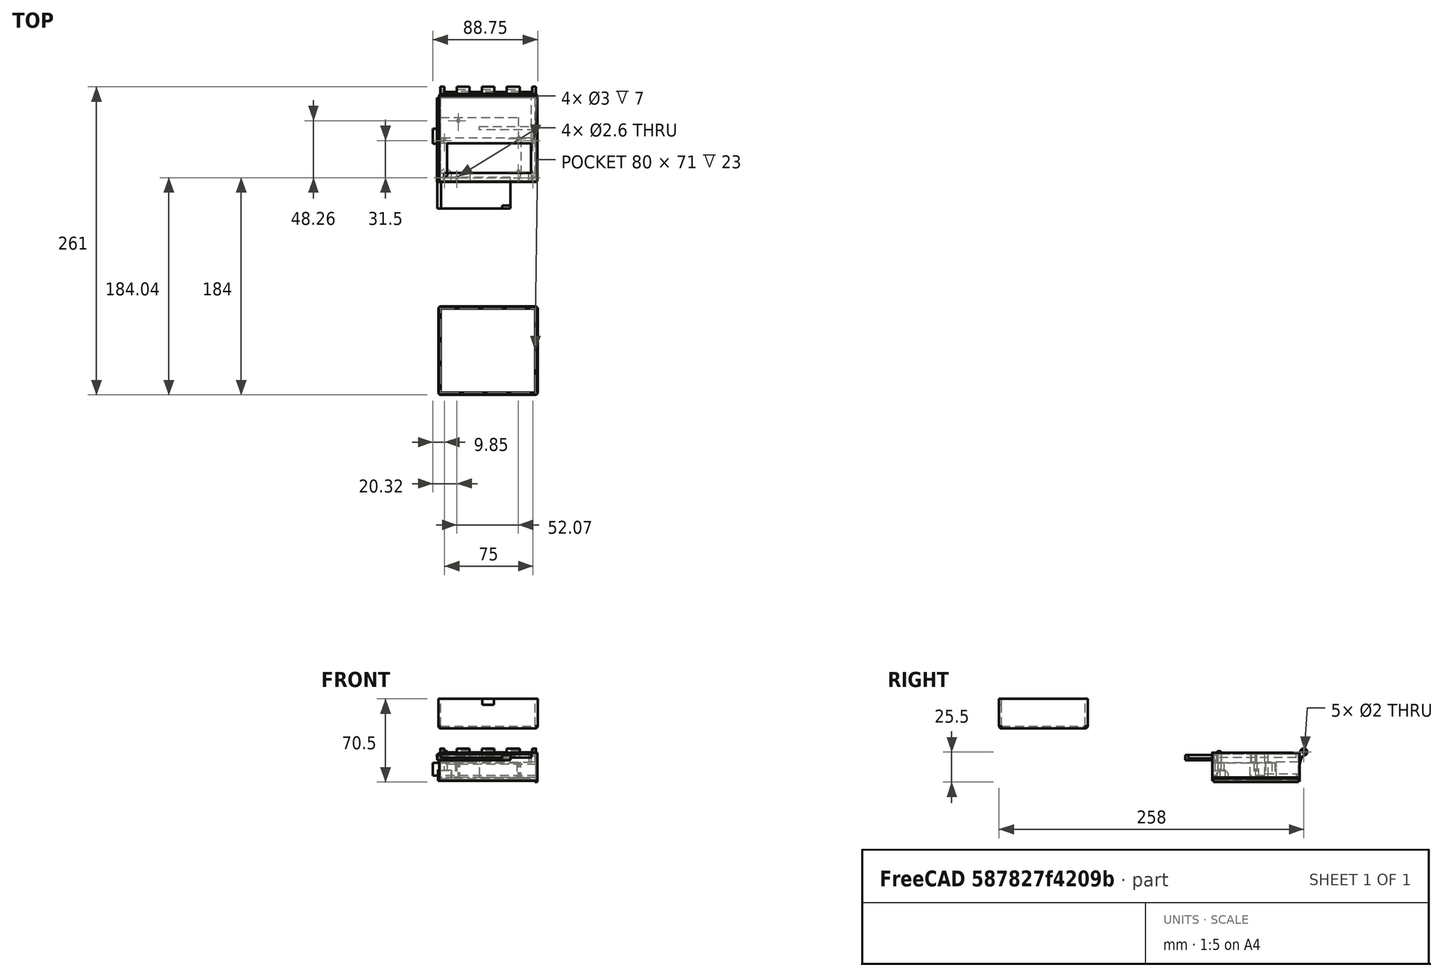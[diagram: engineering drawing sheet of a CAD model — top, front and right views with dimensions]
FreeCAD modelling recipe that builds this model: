
FCSTD DOCUMENT  (FreeCAD 1.0R39109 (Git))
Label: case_top_assembly
License: All rights reserved
LicenseURL: https://en.wikipedia.org/wiki/All_rights_reserved
objects: Sketcher::SketchObject×18, PartDesign::Pad×12, PartDesign::Pocket×8, PartDesign::SubShapeBinder×6, Mesh::Feature×5, PartDesign::Body×5, PartDesign::SubtractiveBox×4, PartDesign::Thickness×2, Part::FeaturePython×2, PartDesign::Fillet×1
note: 130 computed .brp shape members not serialized (recipe doc carries the construction recipe); baked Part::Feature solids carry a one-line shape summary decoded from their .brp

FEATURE [Mesh::Feature] Mesh001  label="power_switch_mesh"
  Placement = pos=(79,9,-82) rot=(0,0,-1;1.5708rad)
FEATURE [Mesh::Feature] Mesh002  label="display_mesh"
  Placement = pos=(-2,11,5) rot=(0,0,1;0rad)
FEATURE [Mesh::Feature] Mesh003  label="9V_Block_mesh"
  Placement = pos=(6,3,0.5) rot=(0,0,-1;1.5708rad)
FEATURE [PartDesign::SubShapeBinder] Binder
  BindCopyOnChange = 0
  BindMode = 0
  ClaimChildren = false
  Context = -> Body001 [Binder.]
  Fuse = false
  MakeFace = true
  OffsetFill = false
  OffsetIntersection = false
  OffsetJoinType = 0
  OffsetOpenResult = false
  PartialLoad = false
  Refine = true
  Relative = true
  Support = -> [b_Electronic_parts_001_003[Edge8,Edge5,Edge2,Edge1]]
  _Version = 2
FEATURE [PartDesign::SubShapeBinder] Binder001
  BindCopyOnChange = 0
  BindMode = 0
  ClaimChildren = false
  Context = -> Body001 [Binder001.]
  Fuse = false
  MakeFace = true
  Offset = 0.5
  OffsetFill = false
  OffsetIntersection = false
  OffsetJoinType = 0
  OffsetOpenResult = false
  PartialLoad = false
  Refine = true
  Relative = true
  Support = -> [b_Electronic_parts_001_002[Face18]]
  _Version = 2
FEATURE [PartDesign::SubShapeBinder] Binder002
  BindCopyOnChange = 0
  BindMode = 0
  ClaimChildren = false
  Context = -> Body001 [Binder002.]
  Fuse = false
  MakeFace = true
  OffsetFill = false
  OffsetIntersection = false
  OffsetJoinType = 0
  OffsetOpenResult = false
  PartialLoad = false
  Refine = true
  Relative = true
  Support = -> [b_Electronic_parts_001_002[Edge34,Edge33,Edge32,Edge31]]
  _Version = 2
FEATURE [Sketcher::SketchObject] Sketch007
  ArcFitTolerance = 1e-06
  AttachmentSupport = -> [XY_Plane001]
  FullyConstrained = true
  MakeInternals = false
  MapMode = 5
  sketch-geometry (4):
    g0: LineSegment StartX=-2.9 StartY=181 StartZ=0 EndX=-2.9 EndY=110 EndZ=0
    g1: LineSegment StartX=-2.9 StartY=110 StartZ=0 EndX=77.1 EndY=110 EndZ=0
    g2: LineSegment StartX=77.1 StartY=110 StartZ=0 EndX=77.1 EndY=181 EndZ=0
    g3: LineSegment StartX=77.1 StartY=181 StartZ=0 EndX=-2.9 EndY=181 EndZ=0
  constraints (10):
    c: Coincident(g0,g1)
    c: Coincident(g1,g2)
    c: Coincident(g2,g3)
    c: Coincident(g3,g0)
    c: Vertical(g0)
    c: Vertical(g2)
    c: Horizontal(g1)
    c: Horizontal(g3)
    c: Coincident(g0,g-4)
    c: Coincident(g1,g-5)
FEATURE [PartDesign::Pad] Pad004
  Direction = (0,0,1)
  Length = 23
  Length2 = 10
  Profile = -> Sketch007
  ReferenceAxis = -> Sketch007 [N_Axis]
  Refine = true
  Suppressed = false
  Type = 0
FEATURE [PartDesign::Thickness] Thickness001
  Base = -> Pad004 [Face6]
  BaseFeature = -> Pad004
  Intersection = false
  Join = 0
  Mode = 0
  Refine = true
  SupportTransform = false
  Suppressed = false
  Value = 2
FEATURE [PartDesign::Pocket] Pocket003
  BaseFeature = -> Thickness001
  Direction = (-1,0,0)
  Length = 5
  Length2 = 5
  Profile = -> Binder001
  Refine = true
  Suppressed = false
  Type = 0
FEATURE [PartDesign::Pocket] Pocket004
  BaseFeature = -> Pocket003
  Direction = (0,0,-1)
  Length = 0
  Length2 = 5
  Profile = -> Binder002
  Refine = true
  Suppressed = false
  Type = 3
  UpToFace = -> Pocket003 [Face19]
FEATURE [Sketcher::SketchObject] Sketch008
  ArcFitTolerance = 1e-06
  AttachmentSupport = -> [Pocket004]
  ExternalGeometry = -> [Pocket004]
  FullyConstrained = true
  MakeInternals = false
  MapMode = 5
  Placement = pos=(0,181,0) rot=(1,0,0;1.5708rad)
  sketch-geometry (6):
    g0: LineSegment StartX=32.1 StartY=23 StartZ=0 EndX=32.1 EndY=18 EndZ=0
    g1: LineSegment StartX=32.1 StartY=18 StartZ=0 EndX=42.1 EndY=18 EndZ=0
    g2: LineSegment StartX=42.1 StartY=18 StartZ=0 EndX=42.1 EndY=23 EndZ=0
    g3: LineSegment StartX=42.1 StartY=23 StartZ=0 EndX=32.1 EndY=23 EndZ=0
    g4: LineSegment [constr] StartX=-2.9 StartY=23 StartZ=0 EndX=32.1 EndY=23 EndZ=0
    g5: LineSegment [constr] StartX=42.1 StartY=23 StartZ=0 EndX=77.1 EndY=23 EndZ=0
  constraints (16):
    c: Coincident(g0,g1)
    c: Coincident(g1,g2)
    c: Coincident(g2,g3)
    c: Coincident(g3,g0)
    c: Vertical(g0)
    c: Vertical(g2)
    c: Horizontal(g1)
    c: Horizontal(g3)
    c: PointOnObject(g0,g-3)
    c: Coincident(g4,g-3)
    c: Coincident(g4,g0)
    c: Coincident(g5,g2)
    c: Coincident(g5,g-3)
    c: Equal(g5,g4)
    c: DistanceX(g1,g1) = 10
    c: DistanceY(g2,g2) = 5
FEATURE [PartDesign::Pocket] Pocket005
  BaseFeature = -> Pocket004
  Direction = (0,1,-2e-16)
  Length = 0
  Length2 = 5
  Profile = -> Sketch008
  ReferenceAxis = -> Sketch008 [N_Axis]
  Refine = true
  Suppressed = false
  Type = 3
  UpToFace = -> Pocket004 [Face14]
FEATURE [Part::FeaturePython] b_Electronic_parts_001_002  label="Electronic_parts_Eleego_002"  # a2plus imported part (geometry in sourceFile) (typed FeaturePython)
  a2p_Version = 0.4.68
  fixedPosition = true
  objectType = a2pPart
  sourceFile = ./Electronic_parts.FCStd
  sourcePart = Eleego
  subassemblyImport = false
  timeLastImport = 1.74161e+09
  updateColors = true
FEATURE [Part::FeaturePython] b_Electronic_parts_001_003  label="Electronic_parts_Keypad_002"  # a2plus imported part (geometry in sourceFile) (typed FeaturePython)
  Placement = pos=(-2.9,70,19.7) rot=(0,0,1;4.71239rad)
  a2p_Version = 0.4.68
  fixedPosition = false
  objectType = a2pPart
  sourceFile = ./Electronic_parts.FCStd
  sourcePart = Keypad
  subassemblyImport = false
  timeLastImport = 1.74161e+09
  updateColors = true
FEATURE [Sketcher::SketchObject] Sketch011
  ArcFitTolerance = 1e-06
  FullyConstrained = true
  MakeInternals = false
  MapMode = 5
  Placement = pos=(0,72,0) rot=(0,0.707107,0.707107;3.14159rad)
  sketch-geometry (12):
    g0: LineSegment StartX=-63.35 StartY=26 StartZ=0 EndX=-52.75 EndY=26 EndZ=0
    g1: LineSegment StartX=-21.35 StartY=26 StartZ=0 EndX=-10.75 EndY=26 EndZ=0
    g2: LineSegment StartX=-63.35 StartY=26 StartZ=0 EndX=-63.35 EndY=17.8 EndZ=0
    g3: LineSegment StartX=-52.75 StartY=26 StartZ=0 EndX=-52.75 EndY=17.8 EndZ=0
    g4: LineSegment StartX=-63.35 StartY=17.8 StartZ=0 EndX=-52.75 EndY=17.8 EndZ=0
    g5: LineSegment [constr] StartX=-74 StartY=26 StartZ=0 EndX=-63.35 EndY=26 EndZ=0
    g6: LineSegment [constr] StartX=-52.75 StartY=26 StartZ=0 EndX=-42.1 EndY=26 EndZ=0
    g7: LineSegment StartX=-21.35 StartY=26 StartZ=0 EndX=-21.35 EndY=17.8 EndZ=0
    g8: LineSegment StartX=-10.75 StartY=26 StartZ=0 EndX=-10.75 EndY=17.8 EndZ=0
    g9: LineSegment StartX=-21.35 StartY=17.8 StartZ=0 EndX=-10.75 EndY=17.8 EndZ=0
    g10: LineSegment [constr] StartX=-32.1 StartY=26 StartZ=0 EndX=-21.35 EndY=26 EndZ=0
    g11: LineSegment [constr] StartX=-10.75 StartY=26 StartZ=0 EndX=0 EndY=26 EndZ=0
  constraints (34):
    c: Horizontal(g0)
    c: Horizontal(g1)
    c: Horizontal(g-6,g0)
    c: Horizontal(g-3,g1)
    c: Distance(g-6,g-4) = 31.9
    c: Coincident(g2,g0)
    c: Vertical(g2)
    c: Coincident(g3,g0)
    c: Vertical(g3)
    c: Coincident(g4,g2)
    c: Coincident(g4,g3)
    c: Parallel(g4,g0)
    c: Coincident(g5,g-6)
    c: Coincident(g5,g0)
    c: Coincident(g6,g0)
    c: Coincident(g6,g-4)
    c: Equal(g5,g6)
    c: DistanceX(g4,g4) = 10.6
    c: Distance(g-6,g-6) = 5.45992
    c: Coincident(g7,g1)
    c: Vertical(g7)
    c: Coincident(g8,g1)
    c: Vertical(g8)
    c: Coincident(g9,g7)
    c: Coincident(g9,g8)
    c: Horizontal(g9)
    c: Coincident(g10,g-3)
    c: Coincident(g10,g1)
    c: Coincident(g11,g1)
    c: Coincident(g11,g-5)
    c: Equal(g11,g10)
    c: Equal(g3,g7)
    c: Equal(g1,g0)
    c: DistanceY(g7,g7) = 8.2
FEATURE [PartDesign::Pocket] Pocket007
  BaseFeature = -> Pocket005
  Direction = (0,-1,2e-16)
  Length = 9
  Length2 = 5
  Profile = -> Sketch011
  ReferenceAxis = -> Sketch011 [N_Axis]
  Refine = true
  Reversed = true
  Suppressed = false
  Type = 0
FEATURE [PartDesign::Body] Body001  label="case_bottom"
  AllowCompound = false
  Group = -> [Sketch007,Binder,Pad004,Thickness001,Binder001,Pocket003,Binder002,Pocket004,Sketch008,Pocket005,Sketch011,Pocket007]
  Origin = -> Origin001
  Placement = pos=(77.5,1.5,46.5) rot=(0,0,1;3.14159rad)
  Tip = -> Pocket007
FEATURE [PartDesign::SubShapeBinder] Binder004
  BindCopyOnChange = 0
  BindMode = 0
  ClaimChildren = false
  Context = -> Body002 [Binder004.]
  Fuse = false
  MakeFace = true
  OffsetFill = false
  OffsetIntersection = false
  OffsetJoinType = 0
  OffsetOpenResult = false
  PartialLoad = false
  Refine = true
  Relative = true
  _Version = 2
FEATURE [Sketcher::SketchObject] Sketch017
  ArcFitTolerance = 1e-06
  AttachmentSupport = -> [XY_Plane002]
  ExternalGeometry = -> [Binder004]
  FullyConstrained = true
  MakeInternals = false
  MapMode = 5
  sketch-geometry (4):
    g0: LineSegment StartX=-2.58093 StartY=2.78 StartZ=0 EndX=-2.58093 EndY=-23.72 EndZ=0
    g1: LineSegment StartX=-2.58093 StartY=-23.72 StartZ=0 EndX=59.4191 EndY=-23.72 EndZ=0
    g2: LineSegment StartX=59.4191 StartY=-23.72 StartZ=0 EndX=59.4191 EndY=2.78 EndZ=0
    g3: LineSegment StartX=59.4191 StartY=2.78 StartZ=0 EndX=-2.58093 EndY=2.78 EndZ=0
  constraints (11):
    c: Coincident(g0,g1)
    c: Coincident(g1,g2)
    c: Coincident(g2,g3)
    c: Coincident(g3,g0)
    c: Vertical(g0)
    c: Vertical(g2)
    c: Horizontal(g1)
    c: Horizontal(g3)
    c: Coincident(g0,g-4)
    c: PointOnObject(g1,g-5)
    c: Vertical(g-3,g2)
FEATURE [PartDesign::Pad] Pad008
  Direction = (0,0,1)
  Length = 1.5
  Length2 = 10
  Profile = -> Sketch017
  ReferenceAxis = -> Sketch017 [N_Axis]
  Refine = true
  Suppressed = false
  Type = 0
FEATURE [Sketcher::SketchObject] Sketch018
  ArcFitTolerance = 1e-06
  AttachmentSupport = -> [Pad008]
  ExternalGeometry = -> [Binder004]
  FullyConstrained = true
  MakeInternals = false
  MapMode = 5
  Placement = pos=(0,0,1.5) rot=(0,0,1;0rad)
  sketch-geometry (11):
    g0: LineSegment StartX=-2.58093 StartY=2.78 StartZ=0 EndX=-2.58093 EndY=-0.22 EndZ=0
    g1: LineSegment StartX=59.4191 StartY=-0.22 StartZ=0 EndX=59.4191 EndY=2.78 EndZ=0
    g2: LineSegment StartX=59.4191 StartY=2.78 StartZ=0 EndX=-2.58093 EndY=2.78 EndZ=0
    g3: LineSegment StartX=0.41907 StartY=-23.72 StartZ=0 EndX=0.41907 EndY=-0.22 EndZ=0
    g4: LineSegment StartX=-2.58093 StartY=-0.22 StartZ=0 EndX=-2.58093 EndY=-23.72 EndZ=0
    g5: LineSegment StartX=-2.58093 StartY=-23.72 StartZ=0 EndX=0.41907 EndY=-23.72 EndZ=0
    g6: LineSegment StartX=59.4191 StartY=-23.72 StartZ=0 EndX=59.4191 EndY=-21.22 EndZ=0
    g7: LineSegment StartX=59.4191 StartY=-21.22 StartZ=0 EndX=52.4191 EndY=-21.22 EndZ=0
    g8: LineSegment StartX=52.4191 StartY=-21.22 StartZ=0 EndX=52.4191 EndY=-23.72 EndZ=0
    g9: LineSegment StartX=52.4191 StartY=-23.72 StartZ=0 EndX=59.4191 EndY=-23.72 EndZ=0
    g10: LineSegment StartX=0.41907 StartY=-0.22 StartZ=0 EndX=59.4191 EndY=-0.22 EndZ=0
  constraints (32):
    c: Coincident(g1,g2)
    c: Coincident(g2,g0)
    c: Vertical(g1)
    c: Horizontal(g2)
    c: Coincident(g0,g-5)
    c: Coincident(g4,g5)
    c: Coincident(g5,g3)
    c: Vertical(g3)
    c: Vertical(g4)
    c: Horizontal(g5)
    c: PointOnObject(g3,g-4)
    c: Vertical(g4,g-5)
    c: Horizontal(g1,g4)
    c: Vertical(g1,g-3)
    c: Coincident(g6,g7)
    c: Coincident(g7,g8)
    c: Coincident(g8,g9)
    c: Coincident(g9,g6)
    c: Vertical(g6)
    c: Vertical(g8)
    c: Horizontal(g7)
    c: Horizontal(g9)
    c: PointOnObject(g6,g-4)
    c: Vertical(g6,g1)
    c: DistanceX(g7,g7) = 7
    c: DistanceY(g8,g8) = 2.5
    c: Coincident(g10,g3)
    c: Coincident(g10,g1)
    c: Horizontal(g10)
    c: Equal(g1,g5)
    c: DistanceY(g1,g1) = 3
    c: Coincident(g0,g4)
FEATURE [PartDesign::Pad] Pad009
  BaseFeature = -> Pad008
  Direction = (0,0,1)
  Length = 3
  Length2 = 10
  Profile = -> Sketch018
  ReferenceAxis = -> Sketch018 [N_Axis]
  Refine = true
  Suppressed = false
  Type = 0
FEATURE [PartDesign::Body] Body002  label="battery_standoff"
  AllowCompound = false
  Group = -> [Binder004,Sketch017,Pad008,Sketch018,Pad009]
  Origin = -> Origin002
  Placement = pos=(0,0,17.5) rot=(0,0,1;0rad)
  Tip = -> Pad009
FEATURE [Sketcher::SketchObject] Sketch019
  ArcFitTolerance = 1e-06
  AttachmentSupport = -> [XY_Plane005]
  FullyConstrained = false
  MakeInternals = false
  MapMode = 5
  sketch-geometry (7):
    g0: ArcOfCircle CenterX=4.5 CenterY=4.95 CenterZ=0 NormalX=0 NormalY=0 NormalZ=1 AngleXU=0 Radius=5.00461 StartAngle=5.83026 EndAngle=9.8777
    g1: LineSegment StartX=0 StartY=2.76 StartZ=0 EndX=0 EndY=0 EndZ=0
    g2: LineSegment StartX=0 StartY=0 StartZ=0 EndX=9 EndY=0 EndZ=0
    g3: LineSegment StartX=9 StartY=0 StartZ=0 EndX=9 EndY=2.76 EndZ=0
    g4: LineSegment [constr] StartX=-0.625057 StartY=10 StartZ=0 EndX=12.7957 EndY=10 EndZ=0
    g5: LineSegment [constr] StartX=-0.511317 StartY=11.1307 StartZ=0 EndX=-0.511317 EndY=0 EndZ=0
    g6: LineSegment [constr] StartX=9.48868 StartY=10.8826 StartZ=0 EndX=9.48868 EndY=0 EndZ=0
  constraints (20):
    c: Horizontal(g0,g0)
    c: Coincident(g1,g2)
    c: Coincident(g2,g3)
    c: Vertical(g1)
    c: Vertical(g3)
    c: Horizontal(g2)
    c: DistanceX(g2,g2) = 9
    c: Horizontal(g4)
    c: Distance(g2,g4) = 10
    c: Coincident(g1,g-1)
    c: Horizontal(g1,g3)
    c: Coincident(g0,g3)
    c: Vertical(g0,g1)
    c: PointOnObject(g5,g-1)
    c: Vertical(g5)
    c: PointOnObject(g6,g-1)
    c: Vertical(g6)
    c: DistanceX(g5,g6) = 10
    c: DistanceY(g-1,g0) = 2.76
    c: DistanceY(g-1,g0) = 4.95
FEATURE [PartDesign::Pad] Pad010
  Direction = (0,0,1)
  Length = 9
  Length2 = 10
  Profile = -> Sketch019
  ReferenceAxis = -> Sketch019 [N_Axis]
  Refine = true
  Suppressed = false
  Type = 0
FEATURE [Sketcher::SketchObject] Sketch009
  ArcFitTolerance = 1e-06
  AttachmentSupport = -> [Pad010]
  ExternalGeometry = -> [Pad010]
  FullyConstrained = true
  MakeInternals = false
  MapMode = 5
  Placement = pos=(0,0,9) rot=(0,0,1;0rad)
  sketch-geometry (1):
    g0: Circle CenterX=4.5 CenterY=4.95 CenterZ=0 NormalX=0 NormalY=0 NormalZ=1 AngleXU=0 Radius=1.5
  constraints (2):
    c: Coincident(g0,g-3)
    c: Radius(g0) = 1.5
FEATURE [PartDesign::Pad] Pad011
  BaseFeature = -> Pad010
  Direction = (0,0,1)
  Length = 16
  Length2 = 10
  Profile = -> Sketch009
  ReferenceAxis = -> Sketch009 [N_Axis]
  Refine = true
  Suppressed = false
  Type = 0
FEATURE [PartDesign::Body] Body005  label="poti"
  AllowCompound = false
  Group = -> [Sketch019,Pad010,Sketch009,Pad011]
  Origin = -> Origin005
  Tip = -> Pad011
FEATURE [Sketcher::SketchObject] Sketch020
  ArcFitTolerance = 1e-06
  AttachmentSupport = -> [XY_Plane006]
  FullyConstrained = true
  MakeInternals = false
  MapMode = 5
  sketch-geometry (4):
    g0: LineSegment StartX=0 StartY=72 StartZ=0 EndX=0 EndY=0 EndZ=0
    g1: LineSegment StartX=0 StartY=0 StartZ=0 EndX=81 EndY=0 EndZ=0
    g2: LineSegment StartX=81 StartY=0 StartZ=0 EndX=81 EndY=72 EndZ=0
    g3: LineSegment StartX=81 StartY=72 StartZ=0 EndX=0 EndY=72 EndZ=0
  constraints (12):
    c: Coincident(g0,g1)
    c: Coincident(g1,g2)
    c: Coincident(g2,g3)
    c: Coincident(g3,g0)
    c: Vertical(g0)
    c: Vertical(g2)
    c: Horizontal(g1)
    c: Horizontal(g3)
    c: PointOnObject(g0,g-2)
    c: PointOnObject(g1,g-1)
    c: DistanceX(g3,g3) = 81
    c: DistanceY(g2,g2) = 72
FEATURE [PartDesign::Pad] Pad012
  Direction = (0,0,1)
  Length = 23
  Length2 = 10
  Profile = -> Sketch020
  ReferenceAxis = -> Sketch020 [N_Axis]
  Refine = true
  Suppressed = false
  Type = 0
FEATURE [PartDesign::Thickness] Thickness002
  Base = -> Pad012 [Face5]
  BaseFeature = -> Pad012
  Intersection = false
  Join = 1
  Mode = 0
  Refine = true
  SupportTransform = false
  Suppressed = false
  Value = 1
FEATURE [PartDesign::Fillet] Fillet001
  Base = -> Thickness002 [Edge19,Edge17,Edge22,Edge20]
  BaseFeature = -> Thickness002
  Radius = 1
  Refine = true
  SupportTransform = false
  Suppressed = false
  UseAllEdges = false
FEATURE [Sketcher::SketchObject] Sketch021
  ArcFitTolerance = 1e-06
  AttachmentSupport = -> [YZ_Plane006]
  ExternalGeometry = -> [Fillet001]
  FullyConstrained = true
  MakeInternals = false
  MapMode = 5
  Placement = pos=(0,0,0) rot=(0.57735,0.57735,0.57735;2.0944rad)
  sketch-geometry (15):
    g0: Circle CenterX=76.5 CenterY=24.5 CenterZ=0 NormalX=0 NormalY=0 NormalZ=1 AngleXU=0 Radius=1
    g1: ArcOfCircle CenterX=76.5 CenterY=24.5 CenterZ=0 NormalX=0 NormalY=0 NormalZ=1 AngleXU=0 Radius=3 StartAngle=4.71239 EndAngle=9.42478
    g2: Circle [constr] CenterX=76.5 CenterY=21.5 CenterZ=0 NormalX=0 NormalY=0 NormalZ=1 AngleXU=0 Radius=1
    g3: Circle [constr] CenterX=74.71 CenterY=21.5 CenterZ=0 NormalX=0 NormalY=0 NormalZ=1 AngleXU=0 Radius=1
    g4: Circle [constr] CenterX=72 CenterY=10.22 CenterZ=0 NormalX=0 NormalY=0 NormalZ=1 AngleXU=0 Radius=1
    g5: BSplineCurve PolesCount=3 KnotsCount=2 Degree=2 IsPeriodic=0
    g6: GeomPoint [constr] X=76.5 Y=21.5 Z=0
    g7: GeomPoint [constr] X=72 Y=10.22 Z=0
    g8: LineSegment StartX=72 StartY=10.22 StartZ=0 EndX=72 EndY=24 EndZ=0
    g9: Circle [constr] CenterX=73.5 CenterY=24.5 CenterZ=0 NormalX=0 NormalY=0 NormalZ=1 AngleXU=0 Radius=1
    g10: Circle [constr] CenterX=73.5 CenterY=24.2 CenterZ=0 NormalX=0 NormalY=0 NormalZ=1 AngleXU=0 Radius=1
    g11: Circle [constr] CenterX=72 CenterY=24 CenterZ=0 NormalX=0 NormalY=0 NormalZ=1 AngleXU=0 Radius=1
    g12: BSplineCurve PolesCount=3 KnotsCount=2 Degree=2 IsPeriodic=0
    g13: GeomPoint [constr] X=73.5 Y=24.5 Z=0
    g14: GeomPoint [constr] X=72 Y=24 Z=0
  constraints (33):
    c: Coincident(g0,g-5)
    c: Radius(g0) = 1
    c: Coincident(g1,g0)
    c: PointOnObject(g1,g-4)
    c: Horizontal(g1,g-6)
    c: Vertical(g0,g1)
    c: Weight(g2) = 1
    c: Equal(g2,g3)
    c: Equal(g2,g4)
    c: InternalAlignment(g2,g5)
    c: InternalAlignment(g3,g5)
    c: InternalAlignment(g4,g5)
    c: InternalAlignment(g6,g5)
    c: InternalAlignment(g7,g5)
    c: Coincident(g2,g1)
    c: PointOnObject(g4,g-7)
    c: Coincident(g8,g5)
    c: DistanceX(g-7,g3) = 2.71
    c: Horizontal(g3,g5)
    c: DistanceY(g-7,g5) = 10.22
    c: Weight(g9) = 1
    c: Equal(g9,g10)
    c: Equal(g9,g11)
    c: InternalAlignment(g9,g12)
    c: InternalAlignment(g10,g12)
    c: InternalAlignment(g11,g12)
    c: InternalAlignment(g13,g12)
    c: InternalAlignment(g14,g12)
    c: Coincident(g9,g1)
    c: Coincident(g11,g8)
    c: Vertical(g10,g12)
    c: DistanceY(g-8,g10) = 0.2
    c: Coincident(g8,g-7)
FEATURE [PartDesign::Pad] Pad013
  BaseFeature = -> Fillet001
  Direction = (1,0,0)
  Length = 81
  Length2 = 10
  Profile = -> Sketch021
  ReferenceAxis = -> Sketch021 [N_Axis]
  Refine = true
  Suppressed = false
  Type = 0
FEATURE [Sketcher::SketchObject] Sketch022
  ArcFitTolerance = 1e-06
  AttachmentSupport = -> [Pad013]
  FullyConstrained = true
  MakeInternals = false
  MapMode = 5
  Placement = pos=(0,72,0) rot=(1,0,0;1.5708rad)
  sketch-geometry (4):
    g0: LineSegment StartX=35.4 StartY=21.5 StartZ=0 EndX=35.4 EndY=19 EndZ=0
    g1: LineSegment StartX=35.4 StartY=19 StartZ=0 EndX=45.4 EndY=19 EndZ=0
    g2: LineSegment StartX=45.4 StartY=19 StartZ=0 EndX=45.4 EndY=21.5 EndZ=0
    g3: LineSegment StartX=45.4 StartY=21.5 StartZ=0 EndX=35.4 EndY=21.5 EndZ=0
  constraints (11):
    c: Coincident(g0,g1)
    c: Coincident(g1,g2)
    c: Coincident(g2,g3)
    c: Coincident(g3,g0)
    c: Vertical(g0)
    c: Vertical(g2)
    c: Horizontal(g1)
    c: Horizontal(g3)
    c: DistanceY(g2,g2) = 2.5
    c: Coincident(g2,g-4)
    c: Vertical(g0,g-5)
FEATURE [PartDesign::Pocket] Pocket
  BaseFeature = -> Pad013
  Direction = (0,1,-2e-16)
  Length = 5
  Length2 = 5
  Profile = -> Sketch022
  ReferenceAxis = -> Sketch022 [N_Axis]
  Refine = true
  Suppressed = false
  Type = 0
FEATURE [PartDesign::SubtractiveBox] Box
  AttacherType = Attacher::AttachEngine3D
  AttachmentOffset = pos=(3.5,73,-4) rot=(0,0,1;0rad)
  AttachmentSupport = -> [Pocket]
  BaseFeature = -> Pocket
  Height = 10
  Length = 10.5
  MapMode = 5
  Placement = pos=(3.5,73,20) rot=(0,0,1;0rad)
  Refine = true
  Suppressed = false
  Width = 10.5
FEATURE [PartDesign::SubtractiveBox] Box001
  AttacherType = Attacher::AttachEngine3D
  AttachmentOffset = pos=(21.3,0,-4) rot=(0,0,1;0rad)
  AttachmentSupport = -> [Box]
  BaseFeature = -> Box
  Height = 10
  Length = 10.5
  MapMode = 5
  Placement = pos=(24.8,73,20) rot=(0,0,1;0rad)
  Refine = true
  Suppressed = false
  Width = 11
FEATURE [PartDesign::SubtractiveBox] Box002
  AttacherType = Attacher::AttachEngine3D
  AttachmentOffset = pos=(20.8,0,-4) rot=(0,0,1;0rad)
  AttachmentSupport = -> [Box001]
  BaseFeature = -> Box001
  Height = 10
  Length = 10.5
  MapMode = 5
  Placement = pos=(45.6,73,20) rot=(0,0,1;0rad)
  Refine = true
  Suppressed = false
  Width = 10
FEATURE [PartDesign::SubtractiveBox] Box003
  AttacherType = Attacher::AttachEngine3D
  AttachmentOffset = pos=(21.5,0,-4) rot=(0,0,1;0rad)
  AttachmentSupport = -> [Box002]
  BaseFeature = -> Box002
  Height = 10
  Length = 10.5
  MapMode = 5
  Placement = pos=(67.1,73,20) rot=(0,0,1;0rad)
  Refine = true
  Suppressed = false
  Width = 10
FEATURE [Sketcher::SketchObject] Sketch
  ArcFitTolerance = 1e-06
  AttachmentSupport = -> [Box003]
  ExternalGeometry = -> [Box003]
  FullyConstrained = true
  MakeInternals = false
  MapMode = 5
  Placement = pos=(67.1,73,23) rot=(1,0,0;3.14159rad)
  sketch-geometry (4):
    g0: LineSegment StartX=-61.5 StartY=66.5 StartZ=0 EndX=-61.5 EndY=41.5 EndZ=0
    g1: LineSegment StartX=-61.5 StartY=41.5 StartZ=0 EndX=9.7 EndY=41.5 EndZ=0
    g2: LineSegment StartX=9.7 StartY=41.5 StartZ=0 EndX=9.7 EndY=66.5 EndZ=0
    g3: LineSegment StartX=9.7 StartY=66.5 StartZ=0 EndX=-61.5 EndY=66.5 EndZ=0
  constraints (12):
    c: Coincident(g0,g1)
    c: Coincident(g1,g2)
    c: Coincident(g2,g3)
    c: Coincident(g3,g0)
    c: Vertical(g0)
    c: Vertical(g2)
    c: Horizontal(g1)
    c: Horizontal(g3)
    c: DistanceY(g2,g2) = 25
    c: DistanceX(g1,g1) = 71.2
    c: DistanceX(g2,g-4) = 4.2
    c: DistanceY(g0,g-5) = 6.5
FEATURE [PartDesign::Pocket] Pocket008
  BaseFeature = -> Box003
  Direction = (0,0,1)
  Length = 0
  Length2 = 5
  Placement = pos=(67.1,73,20) rot=(0,0,1;0rad)
  Profile = -> Sketch
  ReferenceAxis = -> Sketch [N_Axis]
  Refine = true
  Suppressed = false
  Type = 3
  UpToFace = -> Box003 [Face14]
FEATURE [Sketcher::SketchObject] Sketch023
  ArcFitTolerance = 1e-06
  AttachmentSupport = -> [Pocket008]
  ExternalGeometry = -> [Pocket008]
  FullyConstrained = true
  MakeInternals = false
  MapMode = 5
  Placement = pos=(67.1,73,23) rot=(1,0,0;3.14159rad)
  sketch-geometry (16):
    g0: LineSegment StartX=13.9 StartY=73 StartZ=0 EndX=7.9 EndY=73 EndZ=0
    g1: LineSegment StartX=7.9 StartY=73 StartZ=0 EndX=7.9 EndY=66.5 EndZ=0
    g2: LineSegment StartX=7.9 StartY=66.5 StartZ=0 EndX=13.9 EndY=66.5 EndZ=0
    g3: LineSegment StartX=13.9 StartY=66.5 StartZ=0 EndX=13.9 EndY=73 EndZ=0
    g4: LineSegment StartX=-67.1 StartY=73 StartZ=0 EndX=-67.1 EndY=66.5 EndZ=0
    g5: LineSegment StartX=-67.1 StartY=66.5 StartZ=0 EndX=-42.1 EndY=66.5 EndZ=0
    g6: LineSegment StartX=-42.1 StartY=66.5 StartZ=0 EndX=-42.1 EndY=73 EndZ=0
    g7: LineSegment StartX=-42.1 StartY=73 StartZ=0 EndX=-67.1 EndY=73 EndZ=0
    g8: LineSegment StartX=-66.1 StartY=41.5 StartZ=0 EndX=-66.1 EndY=36.5 EndZ=0
    g9: LineSegment StartX=-66.1 StartY=36.5 StartZ=0 EndX=13.9 EndY=36.5 EndZ=0
    g10: LineSegment StartX=13.9 StartY=36.5 StartZ=0 EndX=13.9 EndY=41.5 EndZ=0
    g11: LineSegment StartX=13.9 StartY=41.5 StartZ=0 EndX=-66.1 EndY=41.5 EndZ=0
    g12: Circle CenterX=-63.6 CenterY=39 CenterZ=0 NormalX=0 NormalY=0 NormalZ=1 AngleXU=0 Radius=1.5
    g13: Circle CenterX=11.4 CenterY=39 CenterZ=0 NormalX=0 NormalY=0 NormalZ=1 AngleXU=0 Radius=1.5
    g14: Circle CenterX=-63.6 CenterY=70.5 CenterZ=0 NormalX=0 NormalY=0 NormalZ=1 AngleXU=0 Radius=1.5
    g15: Circle CenterX=11.4 CenterY=70.5 CenterZ=0 NormalX=0 NormalY=0 NormalZ=1 AngleXU=0 Radius=1.5
  constraints (46):
    c: Coincident(g0,g1)
    c: Coincident(g1,g2)
    c: Coincident(g2,g3)
    c: Coincident(g3,g0)
    c: Horizontal(g0)
    c: Horizontal(g2)
    c: Vertical(g1)
    c: Vertical(g3)
    c: Coincident(g0,g-5)
    c: Horizontal(g2,g-6)
    c: DistanceX(g0,g0) = 6
    c: Coincident(g4,g5)
    c: Coincident(g5,g6)
    c: Coincident(g6,g7)
    c: Coincident(g7,g4)
    c: Vertical(g4)
    c: Vertical(g6)
    c: Horizontal(g5)
    c: Horizontal(g7)
    c: Coincident(g4,g-9)
    c: PointOnObject(g5,g-4)
    c: DistanceX(g7,g7) = 25
    c: Coincident(g8,g9)
    c: Coincident(g9,g10)
    c: Coincident(g10,g11)
    c: Coincident(g11,g8)
    c: Vertical(g8)
    c: Vertical(g10)
    c: Horizontal(g9)
    c: Horizontal(g11)
    c: Vertical(g10,g2)
    c: DistanceY(g10,g10) = 5
    c: DistanceX(g9,g9) = 80
    c: Horizontal(g10,g-7)
    c: DistanceX(g8,g12) = 2.5
    c: Radius(g12) = 1.5
    c: DistanceY(g8,g12) = 2.5
    c: Equal(g13,g12)
    c: Horizontal(g12,g13)
    c: DistanceX(g13,g9) = 2.5
    c: Vertical(g12,g14)
    c: Equal(g12,g14)
    c: Equal(g15,g13)
    c: Vertical(g13,g15)
    c: DistanceY(g15,g0) = 2.5
    c: Horizontal(g14,g15)
FEATURE [PartDesign::Pad] Pad
  BaseFeature = -> Pocket008
  Direction = (0,0,-1)
  Length = 7
  Length2 = 10
  Placement = pos=(67.1,73,20) rot=(0,0,1;0rad)
  Profile = -> Sketch023
  ReferenceAxis = -> Sketch023 [N_Axis]
  Refine = true
  Suppressed = false
  Type = 0
FEATURE [Sketcher::SketchObject] Sketch024
  ArcFitTolerance = 1e-06
  AttachmentSupport = -> [Pad]
  ExternalGeometry = -> [Pad]
  FullyConstrained = true
  MakeInternals = false
  MapMode = 5
  Placement = pos=(67.1,73,23) rot=(1,0,0;3.14159rad)
  sketch-geometry (4):
    g0: LineSegment StartX=-34.1 StartY=30 StartZ=0 EndX=-34.1 EndY=27 EndZ=0
    g1: LineSegment StartX=-34.1 StartY=27 StartZ=0 EndX=13.9 EndY=27 EndZ=0
    g2: LineSegment StartX=13.9 StartY=27 StartZ=0 EndX=13.9 EndY=30 EndZ=0
    g3: LineSegment StartX=13.9 StartY=30 StartZ=0 EndX=-34.1 EndY=30 EndZ=0
  constraints (12):
    c: Coincident(g0,g1)
    c: Coincident(g1,g2)
    c: Coincident(g2,g3)
    c: Coincident(g3,g0)
    c: Vertical(g0)
    c: Vertical(g2)
    c: Horizontal(g1)
    c: Horizontal(g3)
    c: Vertical(g1,g-4)
    c: DistanceY(g-4,g1) = 26
    c: DistanceY(g2,g2) = 3
    c: DistanceX(g1,g1) = 48
FEATURE [PartDesign::Pad] Pad014
  BaseFeature = -> Pad
  Direction = (0,0,-1)
  Length = 20
  Length2 = 10
  Placement = pos=(67.1,73,20) rot=(0,0,1;0rad)
  Profile = -> Sketch024
  ReferenceAxis = -> Sketch024 [N_Axis]
  Refine = true
  Suppressed = false
  Type = 0
FEATURE [Sketcher::SketchObject] Sketch025
  ArcFitTolerance = 1e-06
  AttachmentSupport = -> [Pad014]
  ExternalGeometry = -> [Pad014]
  FullyConstrained = true
  MakeInternals = false
  MapMode = 5
  Placement = pos=(0,73,20) rot=(0.57735,0.57735,0.57735;2.0944rad)
  sketch-geometry (4):
    g0: LineSegment StartX=-29 StartY=-4 StartZ=0 EndX=-29 EndY=-13.75 EndZ=0
    g1: LineSegment StartX=-29 StartY=-13.75 StartZ=0 EndX=-1 EndY=-13.75 EndZ=0
    g2: LineSegment StartX=-1 StartY=-13.75 StartZ=0 EndX=-1 EndY=-4 EndZ=0
    g3: LineSegment StartX=-1 StartY=-4 StartZ=0 EndX=-29 EndY=-4 EndZ=0
  constraints (12):
    c: Coincident(g0,g1)
    c: Coincident(g1,g2)
    c: Coincident(g2,g3)
    c: Coincident(g3,g0)
    c: Vertical(g0)
    c: Vertical(g2)
    c: Horizontal(g1)
    c: Horizontal(g3)
    c: DistanceY(g2,g2) = 9.75
    c: DistanceX(g3,g3) = 28
    c: DistanceY(g2,g-5) = 8
    c: Vertical(g1,g-5)
FEATURE [PartDesign::Pocket] Pocket009
  BaseFeature = -> Pad014
  Direction = (-1,0,0)
  Length = 5
  Length2 = 5
  Placement = pos=(67.1,73,20) rot=(0,0,1;0rad)
  Profile = -> Sketch025
  ReferenceAxis = -> Sketch025 [N_Axis]
  Refine = true
  Suppressed = false
  Type = 0
FEATURE [Sketcher::SketchObject] Sketch026
  ArcFitTolerance = 1e-06
  AttachmentSupport = -> [Pocket009]
  ExternalGeometry = -> [Pocket009]
  FullyConstrained = true
  MakeInternals = false
  MapMode = 5
  Placement = pos=(81,73,20) rot=(0.57735,-0.57735,-0.57735;2.0944rad)
  sketch-geometry (28):
    g0: LineSegment StartX=1 StartY=-19 StartZ=0 EndX=1 EndY=-20 EndZ=0
    g1: LineSegment StartX=1 StartY=-20 StartZ=0 EndX=3 EndY=-20 EndZ=0
    g2: LineSegment StartX=3 StartY=-20 StartZ=0 EndX=3 EndY=-19 EndZ=0
    g3: LineSegment StartX=3 StartY=-19 StartZ=0 EndX=1 EndY=-19 EndZ=0
    g4: LineSegment StartX=73 StartY=-20 StartZ=0 EndX=73 EndY=-19 EndZ=0
    g5: LineSegment StartX=73 StartY=-19 StartZ=0 EndX=71 EndY=-19 EndZ=0
    g6: LineSegment StartX=71 StartY=-19 StartZ=0 EndX=71 EndY=-20 EndZ=0
    g7: LineSegment StartX=71 StartY=-20 StartZ=0 EndX=73 EndY=-20 EndZ=0
    g8: LineSegment StartX=1 StartY=-15.5 StartZ=0 EndX=1 EndY=-17 EndZ=0
    g9: LineSegment StartX=1 StartY=-17 StartZ=0 EndX=3 EndY=-17 EndZ=0
    g10: LineSegment StartX=3 StartY=-17 StartZ=0 EndX=3 EndY=-15.5 EndZ=0
    g11: LineSegment StartX=71 StartY=-15.5 StartZ=0 EndX=71 EndY=-17 EndZ=0
    g12: LineSegment StartX=71 StartY=-17 StartZ=0 EndX=73 EndY=-17 EndZ=0
    g13: LineSegment StartX=73 StartY=-17 StartZ=0 EndX=73 EndY=-15.5 EndZ=0
    g14: Circle [constr] CenterX=71 CenterY=-15.5 CenterZ=0 NormalX=0 NormalY=0 NormalZ=1 AngleXU=0 Radius=1
    g15: Circle [constr] CenterX=73 CenterY=-15.5 CenterZ=0 NormalX=0 NormalY=0 NormalZ=1 AngleXU=0 Radius=1
    g16: Circle [constr] CenterX=73 CenterY=-14 CenterZ=0 NormalX=0 NormalY=0 NormalZ=1 AngleXU=0 Radius=1
    g17: BSplineCurve PolesCount=3 KnotsCount=2 Degree=2 IsPeriodic=0
    g18: GeomPoint [constr] X=71 Y=-15.5 Z=0
    g19: GeomPoint [constr] X=73 Y=-14 Z=0
    g20: LineSegment StartX=73 StartY=-14 StartZ=0 EndX=73 EndY=-15.5 EndZ=0
    g21: LineSegment StartX=1 StartY=-15.5 StartZ=0 EndX=1 EndY=-14 EndZ=0
    g22: Circle [constr] CenterX=1 CenterY=-14 CenterZ=0 NormalX=0 NormalY=0 NormalZ=1 AngleXU=0 Radius=1
    g23: Circle [constr] CenterX=1 CenterY=-15.5 CenterZ=0 NormalX=0 NormalY=0 NormalZ=1 AngleXU=0 Radius=1
    g24: Circle [constr] CenterX=3 CenterY=-15.5 CenterZ=0 NormalX=0 NormalY=0 NormalZ=1 AngleXU=0 Radius=1
    g25: BSplineCurve PolesCount=3 KnotsCount=2 Degree=2 IsPeriodic=0
    g26: GeomPoint [constr] X=1 Y=-14 Z=0
    g27: GeomPoint [constr] X=3 Y=-15.5 Z=0
  constraints (71):
    c: Coincident(g0,g1)
    c: Coincident(g1,g2)
    c: Coincident(g2,g3)
    c: Coincident(g3,g0)
    c: Vertical(g0)
    c: Vertical(g2)
    c: Horizontal(g1)
    c: Horizontal(g3)
    c: PointOnObject(g0,g-6)
    c: PointOnObject(g1,g-3)
    c: DistanceY(g2,g2) = 1
    c: DistanceX(g3,g3) = 2
    c: Coincident(g4,g5)
    c: Coincident(g5,g6)
    c: Coincident(g6,g7)
    c: Coincident(g7,g4)
    c: Vertical(g4)
    c: Vertical(g6)
    c: Horizontal(g5)
    c: Horizontal(g7)
    c: Coincident(g4,g-5)
    c: Equal(g5,g3)
    c: Equal(g6,g2)
    c: Coincident(g8,g9)
    c: Coincident(g9,g10)
    c: Horizontal(g9)
    c: Vertical(g8)
    c: Vertical(g10)
    c: Horizontal(g10,g8)
    c: DistanceY(g8,g8) = 1.5
    c: Coincident(g11,g12)
    c: Coincident(g12,g13)
    c: Horizontal(g12)
    c: Vertical(g11)
    c: Vertical(g13)
    c: Horizontal(g13,g11)
    c: Weight(g14) = 1
    c: Equal(g14,g15)
    c: Equal(g14,g16)
    c: InternalAlignment(g14,g17)
    c: InternalAlignment(g15,g17)
    c: InternalAlignment(g16,g17)
    c: InternalAlignment(g18,g17)
    c: InternalAlignment(g19,g17)
    c: Coincident(g14,g11)
    c: Coincident(g20,g17)
    c: Coincident(g20,g13)
    c: Vertical(g20)
    c: DistanceY(g11,g11) = 1.5
    c: DistanceY(g20,g20) = 1.5
    c: Coincident(g15,g13)
    c: DistanceY(g4,g12) = 2
    c: Equal(g5,g9)
    c: Coincident(g21,g8)
    c: PointOnObject(g21,g-6)
    c: Vertical(g21)
    c: DistanceY(g21,g21) = 1.5
    c: Weight(g22) = 1
    c: Equal(g22,g23)
    c: Equal(g22,g24)
    c: InternalAlignment(g22,g25)
    c: InternalAlignment(g23,g25)
    c: InternalAlignment(g24,g25)
    c: InternalAlignment(g26,g25)
    c: InternalAlignment(g27,g25)
    c: Coincident(g22,g21)
    c: Coincident(g24,g10)
    c: Coincident(g23,g8)
    c: DistanceY(g0,g8) = 2
    c: Equal(g5,g12)
    c: Vertical(g12,g4)
FEATURE [PartDesign::Pad] Pad015
  BaseFeature = -> Pocket009
  Direction = (-1,0,0)
  Length = 81
  Length2 = 10
  Placement = pos=(67.1,73,20) rot=(0,0,1;0rad)
  Profile = -> Sketch026
  ReferenceAxis = -> Sketch026 [N_Axis]
  Refine = true
  Suppressed = false
  Type = 0
FEATURE [Sketcher::SketchObject] Sketch027
  ArcFitTolerance = 1e-06
  AttachmentSupport = -> [Pad015]
  ExternalGeometry = -> [Pad015]
  FullyConstrained = true
  MakeInternals = false
  MapMode = 5
  Placement = pos=(81,73,20) rot=(0.57735,-0.57735,-0.57735;2.0944rad)
  sketch-geometry (4):
    g0: LineSegment StartX=1 StartY=-17 StartZ=0 EndX=1 EndY=-20 EndZ=0
    g1: LineSegment StartX=1 StartY=-20 StartZ=0 EndX=73 EndY=-20 EndZ=0
    g2: LineSegment StartX=73 StartY=-20 StartZ=0 EndX=73 EndY=-17 EndZ=0
    g3: LineSegment StartX=73 StartY=-17 StartZ=0 EndX=1 EndY=-17 EndZ=0
  constraints (11):
    c: Coincident(g0,g1)
    c: Coincident(g1,g2)
    c: Coincident(g2,g3)
    c: Coincident(g3,g0)
    c: Vertical(g0)
    c: Vertical(g2)
    c: Horizontal(g1)
    c: Horizontal(g3)
    c: Coincident(g0,g-7)
    c: Vertical(g2,g-4)
    c: DistanceY(g2,g2) = 3
FEATURE [PartDesign::Pocket] Pocket010
  BaseFeature = -> Pad015
  Direction = (1,0,0)
  Length = 5
  Length2 = 5
  Placement = pos=(67.1,73,20) rot=(0,0,1;0rad)
  Profile = -> Sketch027
  ReferenceAxis = -> Sketch027 [N_Axis]
  Refine = true
  Suppressed = false
  Type = 0
FEATURE [PartDesign::Body] Body006  label="case_top_measured"
  AllowCompound = false
  Group = -> [Sketch020,Pad012,Thickness002,Fillet001,Sketch021,Pad013,Sketch022,Pocket,Box,Box001,Box002,Box003,Sketch,Pocket008,Sketch023,Pad,Sketch024,Pad014,Sketch025,Pocket009,Sketch026,Pad015,Sketch027,Pocket010]
  Origin = -> Origin006
  Tip = -> Pocket010
FEATURE [Mesh::Feature] Mesh  label="case_top_mesh"
  Placement = pos=(0,0,-1) rot=(0,0,1;0rad)
FEATURE [PartDesign::SubShapeBinder] Binder005
  BindCopyOnChange = 0
  BindMode = 0
  ClaimChildren = false
  Context = -> Body [Binder005.]
  Fuse = false
  MakeFace = true
  OffsetFill = false
  OffsetIntersection = false
  OffsetJoinType = 0
  OffsetOpenResult = false
  PartialLoad = false
  Refine = true
  Relative = true
  Support = -> [Body006[Pocket010.Edge20,Pocket010.Edge114,Pocket010.Edge4,Pocket010.Edge99,Pocket010.Edge118]]
  _Version = 2
FEATURE [Sketcher::SketchObject] Sketch028
  ArcFitTolerance = 1e-06
  AttachmentSupport = -> [XY_Plane]
  ExternalGeometry = -> [Binder005]
  FullyConstrained = true
  MakeInternals = false
  MapMode = 5
  sketch-geometry (4):
    g0: LineSegment StartX=0 StartY=72 StartZ=0 EndX=0 EndY=0 EndZ=0
    g1: LineSegment StartX=0 StartY=0 StartZ=0 EndX=82 EndY=0 EndZ=0
    g2: LineSegment StartX=82 StartY=0 StartZ=0 EndX=82 EndY=72 EndZ=0
    g3: LineSegment StartX=82 StartY=72 StartZ=0 EndX=0 EndY=72 EndZ=0
  constraints (10):
    c: Coincident(g0,g1)
    c: Coincident(g1,g2)
    c: Coincident(g2,g3)
    c: Coincident(g3,g0)
    c: Vertical(g0)
    c: Vertical(g2)
    c: Horizontal(g1)
    c: Horizontal(g3)
    c: Coincident(g0,g-3)
    c: Coincident(g1,g-8)
FEATURE [PartDesign::Pad] Pad016
  Direction = (0,0,1)
  Length = 2
  Length2 = 10
  Profile = -> Sketch028
  ReferenceAxis = -> Sketch028 [N_Axis]
  Refine = true
  Suppressed = false
  Type = 0
FEATURE [PartDesign::SubShapeBinder] Binder006
  BindCopyOnChange = 0
  BindMode = 0
  ClaimChildren = false
  Context = -> Body [Binder006.]
  Fuse = false
  MakeFace = true
  OffsetFill = false
  OffsetIntersection = false
  OffsetJoinType = 0
  OffsetOpenResult = false
  PartialLoad = false
  Refine = true
  Relative = true
  Support = -> [Body006[Pocket010.Edge27,Pocket010.Edge24]]
  _Version = 2
FEATURE [Sketcher::SketchObject] Sketch029
  ArcFitTolerance = 1e-06
  AttachmentSupport = -> [Pad016]
  ExternalGeometry = -> [Binder006,Pad016]
  FullyConstrained = true
  MakeInternals = false
  MapMode = 5
  Placement = pos=(0,0,0) rot=(1,0,0;3.14159rad)
  sketch-geometry (8):
    g0: LineSegment StartX=82 StartY=0 StartZ=0 EndX=81 EndY=0 EndZ=0
    g1: LineSegment StartX=81 StartY=0 StartZ=0 EndX=81 EndY=-2 EndZ=0
    g2: LineSegment StartX=81 StartY=-2 StartZ=0 EndX=80 EndY=-2 EndZ=0
    g3: LineSegment StartX=82 StartY=-72 StartZ=0 EndX=81 EndY=-72 EndZ=0
    g4: LineSegment StartX=81 StartY=-72 StartZ=0 EndX=81 EndY=-70 EndZ=0
    g5: LineSegment StartX=82 StartY=0 StartZ=0 EndX=82 EndY=-72 EndZ=0
    g6: LineSegment StartX=81 StartY=-70 StartZ=0 EndX=80 EndY=-70 EndZ=0
    g7: LineSegment StartX=80 StartY=-70 StartZ=0 EndX=80 EndY=-2 EndZ=0
  constraints (18):
    c: Coincident(g0,g-5)
    c: Coincident(g0,g-3)
    c: Coincident(g1,g0)
    c: Coincident(g1,g-3)
    c: Coincident(g2,g1)
    c: Horizontal(g2)
    c: Coincident(g3,g-5)
    c: Coincident(g3,g-4)
    c: Coincident(g4,g3)
    c: Coincident(g4,g-4)
    c: Coincident(g5,g0)
    c: Coincident(g5,g3)
    c: Coincident(g6,g4)
    c: Horizontal(g6)
    c: Coincident(g7,g6)
    c: Coincident(g7,g2)
    c: Vertical(g7)
    c: DistanceX(g6,g3) = 2
FEATURE [PartDesign::Pad] Pad017
  BaseFeature = -> Pad016
  Direction = (0,0,-1)
  Length = 1
  Length2 = 10
  Profile = -> Sketch029
  ReferenceAxis = -> Sketch029 [N_Axis]
  Refine = true
  Suppressed = false
  Type = 0
FEATURE [PartDesign::Body] Body  label="lid_top"
  AllowCompound = false
  Group = -> [Sketch028,Binder005,Pad016,Binder006,Sketch029,Pad017]
  Origin = -> Origin
  Tip = -> Pad017
FEATURE [Mesh::Feature] Mesh004  label="lid_top_mesh"
